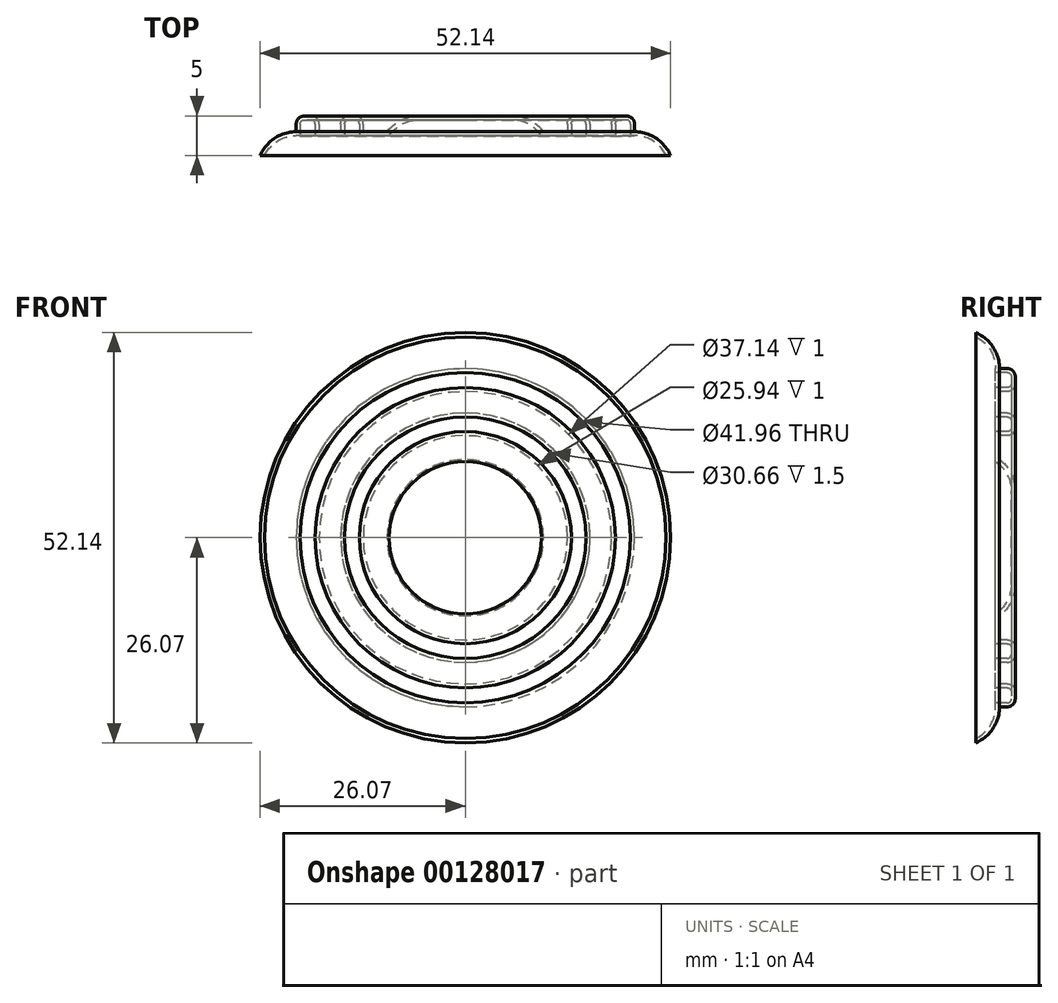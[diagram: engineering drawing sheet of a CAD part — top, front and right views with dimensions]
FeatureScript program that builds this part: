
annotation { "Feature Type Name" : "Feature", "Feature Type Description" : "" }
export const myFeature = defineFeature(function(context is Context, id is Id, definition is map)
    precondition{}
    {
        {
            var Q0;
            Q0=qCreatedBy(makeId("Front.planeOp"),FACE);
            var sketch = newSketch(context, id + "F0", { "sketchPlane" : qUnion([Q0])});
            skCircle(sketch, "E0", {"center": v(0, 0) * mm, "radius": 26.07 * mm});
            skSolve(sketch);
        }
        {
            var Q0;
            Q0=qCreatedBy(makeId("Top.planeOp"),FACE);
            var sketch = newSketch(context, id + "F8", { "sketchPlane" : qUnion([Q0])});
            skLineSegment(sketch, "E1", {"start": v(26.1, 0) * mm, "end": v(33.73, 8.06) * mm});
            skSolve(sketch);
        }
        {
            var Q0;
            Q0=sQuery(id+"F8.wireOp",EDGE,"E1");
            extrude(context, id + "F1", {"bodyType" : ToolBodyType.SURFACE, "surfaceEntities" : qUnion([Q0]), "depth" : 5 * mm});
        }
        {
            var Q0;
            Q0=makeQuery(id+"F1.opExtrude","SWEPT_BODY",BODY,{"disambiguationData":[OSD([sQuery(id+"F8.wireOp",EDGE,"E1")])]});
            var Q1;
            Q1=sQuery(id+"F0.wireOp",EDGE,"E0");
            circularPattern(context, id + "F2", {"entities" : qUnion([Q0]), "axis" : qUnion([Q1]), "angle" : 360 * degree, "instanceCount" : 30, "equalSpace" : true});
        }
        {
            var Q0;
            Q0=makeQuery(id+"F0.imprint","IMPRINT",FACE,{"disambiguationData":[TD([[makeQuery(id+"F0.imprint","IMPRINT",EDGE,{"derivedFrom":sQuery(id+"F0.wireOp",EDGE,"E0")}),1.0]])]});
            extrude(context, id + "F9", {"entities" : qUnion([Q0]), "oppositeDirection" : true, "depth" : 3 * mm});
        }
        {
            var Q0;
            Q0=makeQuery(id+"F9.opExtrude","CAP_FACE",FACE,{"disambiguationData":[OSD([sQuery(id+"F0.wireOp",EDGE,"E0")])],"isStart":false});
            var Q1;
            Q1=makeQuery(id+"F9.opExtrude","CAP_EDGE",EDGE,{"disambiguationData":[OSD([sQuery(id+"F0.wireOp",EDGE,"E0")])],"isStart":false});
            fillet(context, id + "F3", {"entities" : qUnion([Q0, Q1]), "radius" : 5 * mm, "tangentPropagation" : true, "allowEdgeOverflow" : false});
        }
        {
            var Q0;
            Q0=makeQuery(id+"F9.opExtrude","CAP_FACE",FACE,{"disambiguationData":[OSD([sQuery(id+"F0.wireOp",EDGE,"E0")])],"isStart":false});
            var sketch = newSketch(context, id + "F4", { "sketchPlane" : qUnion([Q0])});
            skCircle(sketch, "E2", {"center": v(0, 0) * mm, "radius": 18.57 * mm});
            skCircle(sketch, "E3", {"center": v(0, 0) * mm, "radius": 15.83 * mm});
            skCircle(sketch, "E4", {"center": v(0, 0) * mm, "radius": 12.97 * mm});
            skCircle(sketch, "E5", {"center": v(0, 0) * mm, "radius": 9.93 * mm});
            skSolve(sketch);
        }
        {
            var Q0;
            Q0=makeQuery(id+"F4.imprint","IMPRINT",FACE,{"disambiguationData":[TD([[makeQuery(id+"F4.imprint","IMPRINT",EDGE,{"derivedFrom":sQuery(id+"F4.wireOp",EDGE,"E5")}),1.0]])]});
            var Q1;
            Q1=makeQuery(id+"F4.imprint","IMPRINT",FACE,{"disambiguationData":[TD([[makeQuery(id+"F4.imprint","IMPRINT",EDGE,{"derivedFrom":sQuery(id+"F4.wireOp",EDGE,"E3")}),1.0]])]});
            var Q2;
            Q2=makeQuery(id+"F4.imprint","IMPRINT",FACE,{"disambiguationData":[TD([[makeQuery(id+"F4.imprint","IMPRINT",EDGE,{"derivedFrom":sQuery(id+"F4.wireOp",EDGE,"E2")}),-1.0]])]});
            extrude(context, id + "F5", {"entities" : qUnion([Q0, Q1, Q2]), "operationType" : NewBodyOperationType.ADD, "depth" : 2 * mm});
        }
        {
            var Q0;
            Q0=makeQuery(id+"F5.opExtrude","CAP_FACE",FACE,{"disambiguationData":[OSD([sQuery(id+"F4.wireOp",EDGE,"E5")])],"isStart":false});
            fillet(context, id + "F10", {"entities" : qUnion([Q0]), "radius" : 5 * mm, "tangentPropagation" : true, "allowEdgeOverflow" : false});
        }
        {
            var Q0;
            Q0=makeQuery(id+"F5.opExtrude","CAP_EDGE",EDGE,{"disambiguationData":[OSD([sQuery(id+"F4.wireOp",EDGE,"E4")])],"isStart":false});
            var Q1;
            Q1=makeQuery(id+"F5.opExtrude","CAP_EDGE",EDGE,{"disambiguationData":[OSD([sQuery(id+"F4.wireOp",EDGE,"E3")])],"isStart":false});
            var Q2;
            Q2=makeQuery(id+"F5.opExtrude","CAP_EDGE",EDGE,{"disambiguationData":[OSD([sQuery(id+"F4.wireOp",EDGE,"E2")])],"isStart":false});
            var Q3;
            Q3=makeQuery(id+"F5.opExtrude","CAP_EDGE",EDGE,{"disambiguationData":[OSD([sQuery(id+"F0.wireOp",EDGE,"E0")])],"isStart":false});
            fillet(context, id + "F6", {"entities" : qUnion([Q0, Q1, Q2, Q3]), "radius" : 1 * mm, "tangentPropagation" : true, "allowEdgeOverflow" : false});
        }
        {
            var Q0;
            Q0=makeQuery(id+"F9.opExtrude","CAP_FACE",FACE,{"disambiguationData":[OSD([sQuery(id+"F0.wireOp",EDGE,"E0")])],"isStart":true});
            shell(context, id + "F7", {"entities" : qUnion([Q0]), "thickness" : 0.5 * mm});
        }
    });
